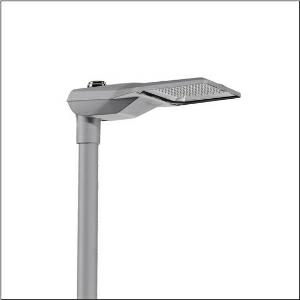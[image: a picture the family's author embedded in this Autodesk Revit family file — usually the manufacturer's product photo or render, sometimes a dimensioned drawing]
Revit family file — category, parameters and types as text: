
# Revit family: streetlight_sl_21_midi___st0_8a_5xe7c37n08lb_f1b7
name_source: partatom
category: Lighting Fixtures
units: mm (PartAtom-declared; Revit-internal decimal feet)

## family parameters
Cut with Voids When Loaded = No
Host = Face
Light Source = No
Part Type = Normal
Room Calculation Point = No
Round Connector Dimension = Use Diameter
Shared = No

## types (1)
- --- (1 x LED, 14340 lm, 98.3 W, 3000K)
    Apparent Load = 98 VA
    CIE Flux Codes = 38 75 97 100 100
    Color Rendering = 70
    Color Temperature = 3000K
    Default Elevation = 1800 mm
    Description = Streetlight SL 21 midi, mast luminaire, primary light control with lens, of PMMA, primary optical cover: cover, of toughened safety glass, transparent, light distribution: ST0.8a, light emission: direct distribution, primary light characteristic: asymmetric, installation type: side-entry, LED, 3G 2.5mm², High Power LED, rated luminous flux: 14.340lm, luminous efficacy: 146lm/W, light colour: 730, colour temperature: 3000K, control gear: NEMA (7pin), control: overheat protection, pre-setting: linear dimming characteristic, constant luminous flux control, time-dependent luminous flux control, flexible luminous flux parameterisation, mains connection: 220..240V, AC, 50/60Hz, connection cable pre-assembled, cable length: 10,5m, wiring characteristics: H05VV-F, start of lifetime: 98W, end of service life: 101W, reduction: 45W, luminaire housing, of diecast aluminium (EN AC-44300), powder-coated, Siteco® metallic grey (DB 702S), corrosivity category C5 mid according to DIN EN ISO 12944, multi-level sealing system, sealing non-destructively replaceable, inclination adjustable: 0°, 5°, 10°, 15°, length: 644mm, width: 335mm, height: 110mm, spigot size: 42mm (side-entry), mounting height: 4..8m, protection rating (complete): IP66, insulation class (complete): insulation class I (protective earthing), certification: CE, ENEC, ENEC+, VDE, impact resistance: IK10, permissible operating ambient temperature for outdoor applications: -40..+50°C, standard-compliant lighting for roads and squares, packaging unit: 1 piece

Light Distribution: ST0.8a
    Height = 111 mm
    Lamp = 1 x LED
    Lamp Light Flux = 14340 lm
    Lamp Power = 98.3 W
    Lamp count = 1
    Length = 644 mm
    Luminous efficacy = 146 lm/W
    Manufacturer = Siteco
    ModVariant = No
    Model = 5XE7C37N08LB
    Number of Poles = 1
    OnlyDefault = Yes
    Power Factor = 1
    Product Name = Streetlight SL 21 midi | ST0.8a
    Product group = mast luminaire | pylon top
    ProductGroupID = 6100
    Protection Class = Protection class I
    Protection Degree = IP 66
    RLX_Detail_Level = 1
    RLX_Emergency_Light_Flux = 0 lm
    RLX_Emergency_Type = 0
    RLX_Emergency_Type_DB = No
    RlxData = <blob elided: 26733 chars, md5=cf2964fd>
    Socket = socket
    Standby Power = 0 W
    System Light Flux = 14340 lm
    System Power = 98 W
    Type Comments = factory setting: luminous flux: 100 % | dim-lin: 254 | 1020 mA
    Type Image = l_1294377.jpg
    URL = http://relux.com
    VarID = @adj_155587
    Voltage = 0 V
    Weight = 0.00 kg
    Width = 336 mm

## geometry (parser evidence)
native form markers: Blend x4, Sweep x11
no freeform markers — native parametric forms only
